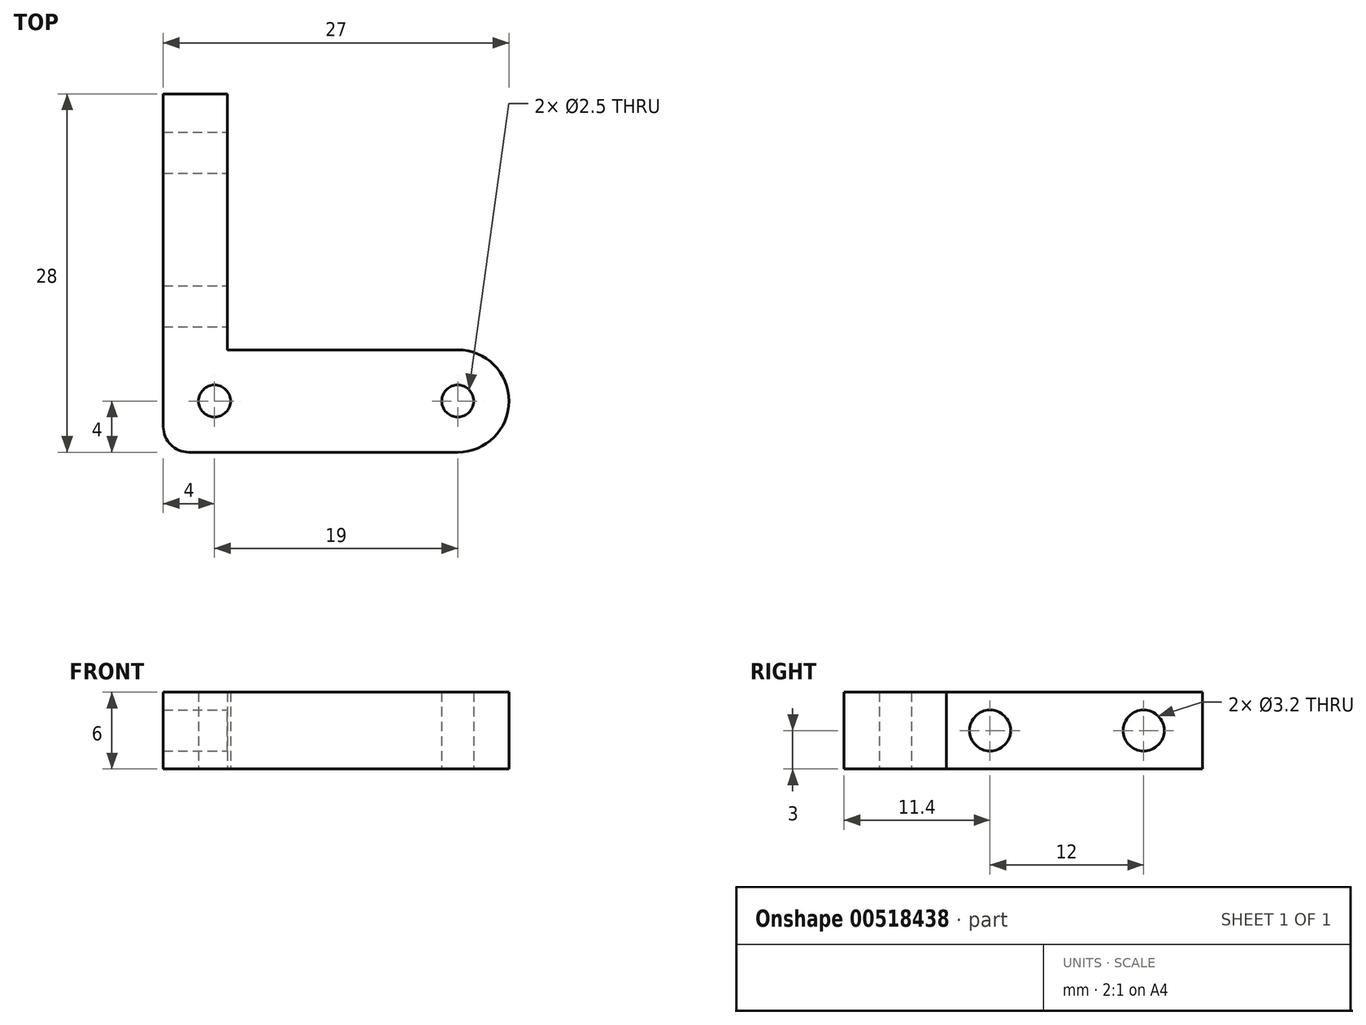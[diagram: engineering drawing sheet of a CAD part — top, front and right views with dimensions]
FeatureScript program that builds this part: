
annotation { "Feature Type Name" : "Feature", "Feature Type Description" : "" }
export const myFeature = defineFeature(function(context is Context, id is Id, definition is map)
    precondition{}
    {
        {
            var Q0;
            Q0=qCreatedBy(makeId("Top.planeOp"),FACE);
            var sketch = newSketch(context, id + "F0", { "sketchPlane" : qUnion([Q0])});
            skPoint(sketch, "E0.middle", {"position": v(0, 0) * mm});
            skLineSegment(sketch, "E1", {"start": v(-5, -10) * mm, "end": v(-2, -10) * mm});
            skLineSegment(sketch, "E2", {"start": v(17, -14) * mm, "end": v(17, -14) * mm});
            skLineSegment(sketch, "E3", {"start": v(13, -18) * mm, "end": v(2, -18) * mm});
            skLineSegment(sketch, "E4", {"start": v(-10, -16) * mm, "end": v(-10, -10) * mm});
            skLineSegment(sketch, "E5.trimOffspring", {"start": v(2, -10) * mm, "end": v(13, -10) * mm});
            skPoint(sketch, "E6.visualSharp", {"position": v(-10, -10) * mm});
            skLineSegment(sketch, "E6.filletArc", {"start": v(-10, -10) * mm, "end": v(-10, -10) * mm});
            skPoint(sketch, "E7.visualSharp", {"position": v(-10, -18) * mm});
            skLineSegment(sketch, "E7.filletArc", {"start": v(-10, -18) * mm, "end": v(-10, -18) * mm});
            skPoint(sketch, "E8.visualSharp", {"position": v(17, -10) * mm});
            skArc(sketch, "E8.filletArc", {"start": v(17, -14) * mm, "mid": v(15.83, -11.17) * mm, "end": v(13, -10) * mm});
            skPoint(sketch, "E9.visualSharp", {"position": v(17, -18) * mm});
            skArc(sketch, "E9.filletArc", {"start": v(13, -18) * mm, "mid": v(15.83, -16.83) * mm, "end": v(17, -14) * mm});
            skCircle(sketch, "E10", {"center": v(13, -14) * mm, "radius": 1.25 * mm});
            skLineSegment(sketch, "E11", {"start": v(-6, -27.41) * mm, "end": v(-6, -27.41) * mm});
            skPoint(sketch, "E12.visualSharp", {"position": v(-10, -27.41) * mm});
            skPoint(sketch, "E13.visualSharp", {"position": v(-2, -27.41) * mm});
            skPoint(sketch, "E14.visualSharp", {"position": v(-2, -18) * mm});
            skCircle(sketch, "E15", {"center": v(-6, -14) * mm, "radius": 1.25 * mm});
            skLineSegment(sketch, "E16", {"start": v(-10, -10) * mm, "end": v(-10, 10) * mm});
            skLineSegment(sketch, "E17", {"start": v(-10, 10) * mm, "end": v(-5, 10) * mm});
            skLineSegment(sketch, "E18", {"start": v(-5, 10) * mm, "end": v(-5, -10) * mm});
            skLineSegment(sketch, "E19", {"start": v(-2, -10) * mm, "end": v(2, -10) * mm});
            skPoint(sketch, "E0.right.end.orphan", {"position": v(-2, 10) * mm});
            skPoint(sketch, "E0.left.end.orphan", {"position": v(2, 10) * mm});
            skLineSegment(sketch, "E20", {"start": v(2, -18) * mm, "end": v(-8, -18) * mm});
            skArc(sketch, "E21.filletArc", {"start": v(-10, -16) * mm, "mid": v(-9.41, -17.41) * mm, "end": v(-8, -18) * mm});
            skSolve(sketch);
        }
        {
            var Q0;
            Q0=makeQuery(id+"F0.imprint","IMPRINT",FACE,{"disambiguationData":[TD([[makeQuery(id+"F0.imprint","IMPRINT",EDGE,{"derivedFrom":sQuery(id+"F0.wireOp",EDGE,"E1")}),-1.0]])]});
            extrude(context, id + "F1", {"entities" : qUnion([Q0]), "depth" : 6 * mm, "offsetDistance" : 25 * mm});
        }
        {
            var Q0;
            Q0=makeQuery(id+"F1.opExtrude","SWEPT_FACE",FACE,{"disambiguationData":[OSD([sQuery(id+"F0.wireOp",EDGE,"E18")])]});
            var sketch = newSketch(context, id + "F2", { "sketchPlane" : qUnion([Q0])});
            skCircle(sketch, "E22", {"center": v(5.4, 3) * mm, "radius": 1.6 * mm});
            skCircle(sketch, "E23", {"center": v(-6.6, 3) * mm, "radius": 1.6 * mm});
            skSolve(sketch);
        }
        {
            var Q0;
            Q0=makeQuery(id+"F2.imprint","IMPRINT",FACE,{"disambiguationData":[TD([[makeQuery(id+"F2.imprint","IMPRINT",EDGE,{"derivedFrom":sQuery(id+"F2.wireOp",EDGE,"E22")}),1.0]])]});
            var Q1;
            Q1=makeQuery(id+"F2.imprint","IMPRINT",FACE,{"disambiguationData":[TD([[makeQuery(id+"F2.imprint","IMPRINT",EDGE,{"derivedFrom":sQuery(id+"F2.wireOp",EDGE,"E23")}),1.0]])]});
            extrude(context, id + "F3", {"entities" : qUnion([Q0, Q1]), "operationType" : NewBodyOperationType.REMOVE, "endBound" : BoundingType.THROUGH_ALL, "oppositeDirection" : true, "depth" : 25 * mm, "offsetDistance" : 25 * mm});
        }
    });
